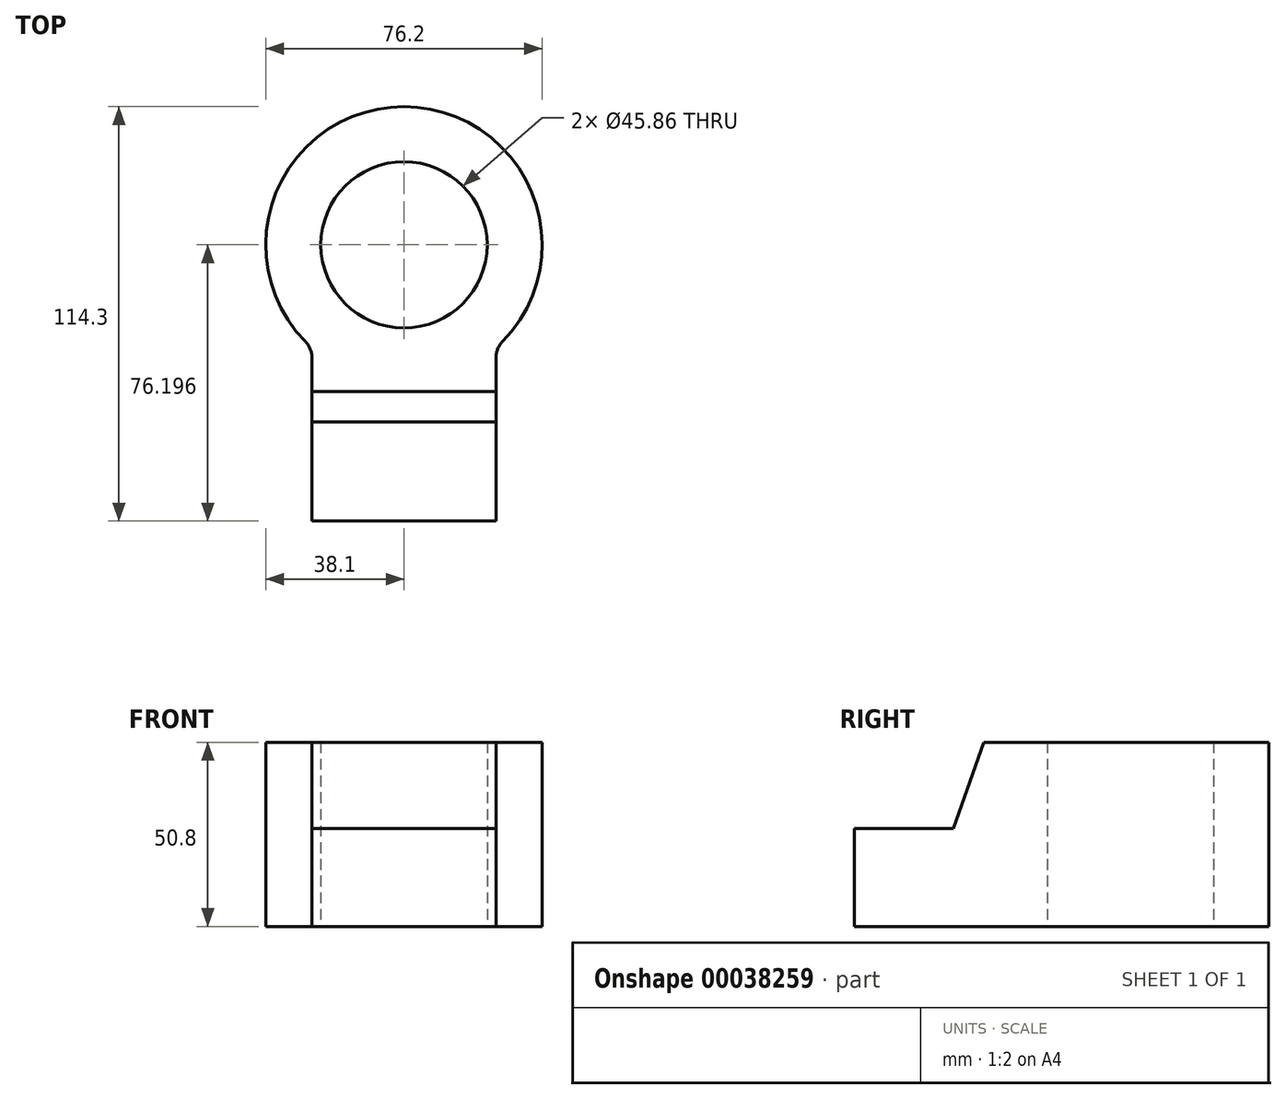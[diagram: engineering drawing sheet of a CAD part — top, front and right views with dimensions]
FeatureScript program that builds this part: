
annotation { "Feature Type Name" : "Feature", "Feature Type Description" : "" }
export const myFeature = defineFeature(function(context is Context, id is Id, definition is map)
    precondition{}
    {
        {
            var Q0;
            Q0=qCreatedBy(makeId("Top.planeOp"),FACE);
            var sketch = newSketch(context, id + "F0", { "sketchPlane" : qUnion([Q0])});
            skArc(sketch, "E0", {"start": v(27.2, 6.9) * mm, "mid": v(0, 71.69) * mm, "end": v(-27.2, 6.9) * mm});
            skLineSegment(sketch, "E1.bottom", {"start": v(-25.38, -42.61) * mm, "end": v(25.38, -42.61) * mm});
            skLineSegment(sketch, "E1.left", {"start": v(-25.38, -42.61) * mm, "end": v(-25.38, 2.45) * mm});
            skLineSegment(sketch, "E1.right", {"start": v(25.38, -42.61) * mm, "end": v(25.38, 2.45) * mm});
            skPoint(sketch, "E2.visualSharp", {"position": v(-25.38, 5.17) * mm});
            skArc(sketch, "E2.filletArc", {"start": v(-25.38, 2.45) * mm, "mid": v(-25.85, 4.86) * mm, "end": v(-27.2, 6.9) * mm});
            skPoint(sketch, "E3.visualSharp", {"position": v(25.38, 5.17) * mm});
            skArc(sketch, "E3.filletArc", {"start": v(27.2, 6.9) * mm, "mid": v(25.85, 4.86) * mm, "end": v(25.38, 2.45) * mm});
            skCircle(sketch, "E4", {"center": v(0, 33.59) * mm, "radius": 22.93 * mm});
            skSolve(sketch);
        }
        {
            var Q0;
            Q0=makeQuery(id+"F0.imprint","IMPRINT",FACE,{"disambiguationData":[TD([[makeQuery(id+"F0.imprint","IMPRINT",EDGE,{"derivedFrom":sQuery(id+"F0.wireOp",EDGE,"E0")}),1.0]])]});
            extrude(context, id + "F1", {"entities" : qUnion([Q0]), "depth" : 50.8 * mm});
        }
        {
            var Q0;
            Q0=qCreatedBy(makeId("Right.planeOp"),FACE);
            var sketch = newSketch(context, id + "F2", { "sketchPlane" : qUnion([Q0])});
            skLineSegment(sketch, "E5", {"start": v(-42.94, 27.03) * mm, "end": v(-15.26, 27.03) * mm});
            skLineSegment(sketch, "E6", {"start": v(-15.26, 27.03) * mm, "end": v(-4.36, 57.76) * mm});
            skLineSegment(sketch, "E7", {"start": v(-4.36, 57.76) * mm, "end": v(-47.52, 57.76) * mm});
            skLineSegment(sketch, "E8", {"start": v(-47.52, 57.76) * mm, "end": v(-47.52, 27.25) * mm});
            skLineSegment(sketch, "E9", {"start": v(-47.52, 27.25) * mm, "end": v(-42.94, 27.03) * mm});
            skSolve(sketch);
        }
        {
            var Q0;
            Q0=makeQuery(id+"F2.imprint","IMPRINT",FACE,{"disambiguationData":[TD([[makeQuery(id+"F2.imprint","IMPRINT",EDGE,{"derivedFrom":sQuery(id+"F2.wireOp",EDGE,"E5")}),1.0]])]});
            extrude(context, id + "F3", {"entities" : qUnion([Q0]), "operationType" : NewBodyOperationType.REMOVE, "endBound" : BoundingType.SYMMETRIC, "oppositeDirection" : true, "depth" : 76.2 * mm});
        }
    });
